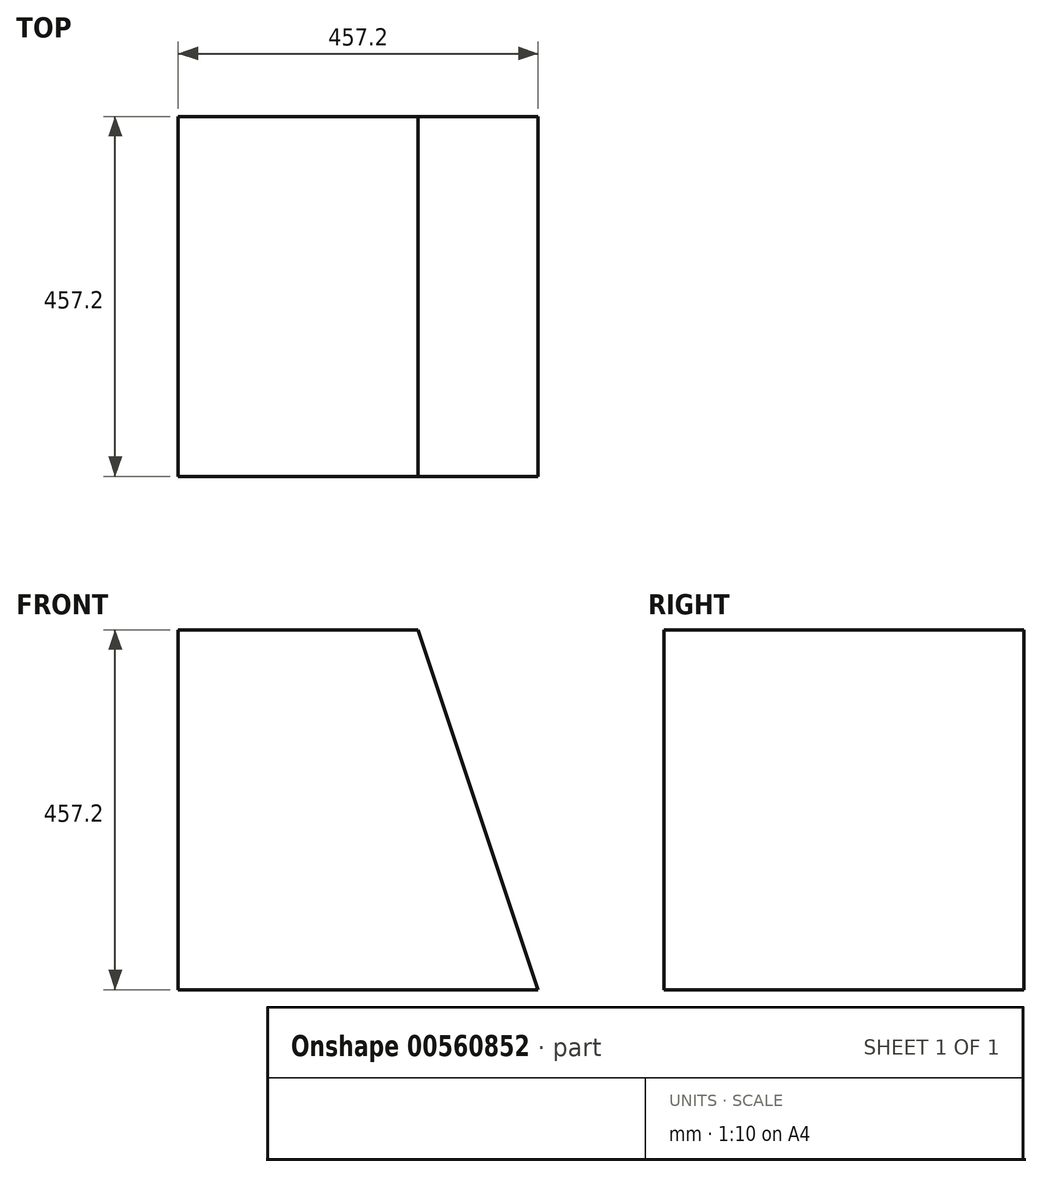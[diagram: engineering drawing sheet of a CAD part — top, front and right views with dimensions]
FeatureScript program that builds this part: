
annotation { "Feature Type Name" : "Feature", "Feature Type Description" : "" }
export const myFeature = defineFeature(function(context is Context, id is Id, definition is map)
    precondition{}
    {
        {
            var Q0;
            Q0=qCreatedBy(makeId("Front.planeOp"),FACE);
            var sketch = newSketch(context, id + "F0", { "sketchPlane" : qUnion([Q0])});
            skLineSegment(sketch, "E0", {"start": v(-217.66, 341.21) * mm, "end": v(-217.66, -115.99) * mm});
            skLineSegment(sketch, "E1", {"start": v(-217.66, 341.21) * mm, "end": v(87.14, 341.21) * mm});
            skLineSegment(sketch, "E2", {"start": v(87.14, 341.21) * mm, "end": v(239.54, -115.99) * mm});
            skLineSegment(sketch, "E3", {"start": v(-217.66, -115.99) * mm, "end": v(239.54, -115.99) * mm});
            skSolve(sketch);
        }
        {
            var Q0;
            Q0 = qSketchRegion(id + "F0", true);
            extrude(context, id + "F1", {"entities" : qUnion([Q0]), "depth" : 457.2 * mm, "offsetDistance" : 25.4 * mm});
        }
    });
